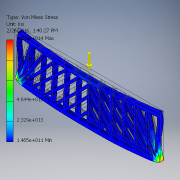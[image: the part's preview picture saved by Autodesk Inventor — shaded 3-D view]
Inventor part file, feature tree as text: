
AUTODESK INVENTOR PART (.ipt)
format: ipt  version: 2016 (Build 200138000, 138)  size: 526,848 bytes
history: native  units: in
note: dims shown in document units (in); Inventor stores cm internally (conversion verified against a paired STEP export)
features: extrude x1, sketch x1, other x1
ambient origin geometry x8: Origin, YZ Plane, XZ Plane, XY Plane, X Axis, Y Axis, Z Axis, Center Point
bodies: Solid1 (feature_tree)
feature tree (3):
  extrude  "Extrusion1"  Depth=2.014in
  sketch  "Sketch1"  dims[d162=0.125in d163=0.0in d165=0.1186in d166=0.1116in d167=0.2004in d168=0.2657in d169=0.3036in d170=0.3023in d171=0.3037in d172=0.3057in d173=0.3042in d174=0.3057in d175=0.2993in d176=0.3057in d177=0.2719in d178=0.209in d179=0.0009in d180=0.0009in d181=0.0009in d182=0.1133in d183=0.1162in d184=0.101in d185=0.1778in d186=0.5115in d187=0.5115in d188=0.5812in d189=0.5812in d190=0.5812in d191=0.912in d192=0.912in d193=0.912in d194=0.9901in d195=0.9901in d196=0.9901in d197=1.3416in d198=1.3416in d199=1.3416in d200=1.411in d201=1.411in d202=1.411in d203=1.7445in d204=1.7445in d205=1.7445in d206=1.7445in d207=1.817in d208=1.817in d209=1.8171in d210=2.1666in d211=2.1666in d212=2.1666in d213=2.2235in d214=2.2235in d215=2.2235in d216=2.5633in d217=2.5633in d218=2.5633in d219=2.5633in d220=2.6361in d221=2.6361in d222=2.6361in d223=2.6361in d224=2.9632in d225=2.9632in d226=2.9632in d227=3.0359in d228=3.0359in d229=3.0359in d230=3.0359in d231=3.3814in d232=3.3814in d233=3.3814in d234=3.4553in d235=3.4553in d236=3.4553in d237=3.8023in d238=3.8023in d239=3.8023in d240=3.8799in d241=3.8799in d242=3.8799in d243=4.2065in d244=4.2065in d245=4.2065in d246=4.2682in d247=4.2682in d248=4.2682in d249=4.2682in d250=4.6759in d251=4.6759in d252=4.6759in d253=5.0288in d254=5.0872in d255=5.2083in d256=1.2144in d257=0.0in d258=1.2144in d259=0.0in d260=1.2144in d261=0.0in d262=1.2144in d263=0.0019in d264=1.2144in d265=0.0in d266=1.2144in d267=0.1203in d268=1.3341in d269=0.2128in d270=1.2144in d271=0.0in d272=1.2144in d273=0.0in d274=1.2144in d275=0.0in d276=1.2144in d277=1.2144in d278=0.0in d279=1.2144in d280=1.2144in d281=0.0in d282=1.2144in d283=0.0in d284=0.0817in d285=0.0in d286=0.0817in d287=0.0614in d288=0.0in d289=0.0614in d290=0.0in d291=0.0614in d292=0.0695in d293=0.0in d294=0.0695in d295=0.2933in d296=0.3551in d297=0.0in d298=0.0695in d299=0.2933in d300=0.3551in d301=0.3551in d302=0.8303in d303=0.292in d304=0.8303in d305=0.0741in d306=0.0in d307=0.0741in d308=0.3052in d309=0.0in d310=0.0741in d311=0.3052in d312=0.5484in d313=0.6232in d314=0.3918in d315=0.321in d316=0.0759in d317=0.321in d318=0.3918in d319=0.3745in d320=0.2984in d321=0.0in d322=0.0in d323=0.3745in d324=0.2984in d325=0.2984in d326=0.3745in d327=0.0716in d328=0.0716in d329=0.0in d330=0.0in d331=0.0716in d332=0.0715in d333=0.0in d334=0.0715in d335=0.0715in d336=0.0in d337=0.0716in d338=0.0in d339=0.0716in d340=4.4223in d341=4.3761in d342=3.6481in d343=2.9185in d344=2.3238in d345=1.7403in d346=2.6436in d347=2.014in d348=2.0916in d349=2.014in d350=1.4887in d351=2.014in d352=1.1596in d353=1.0027in d354=0.6016in d355=0.6016in d356=0.6016in d357=0.5622in]
  other  "Image1"
